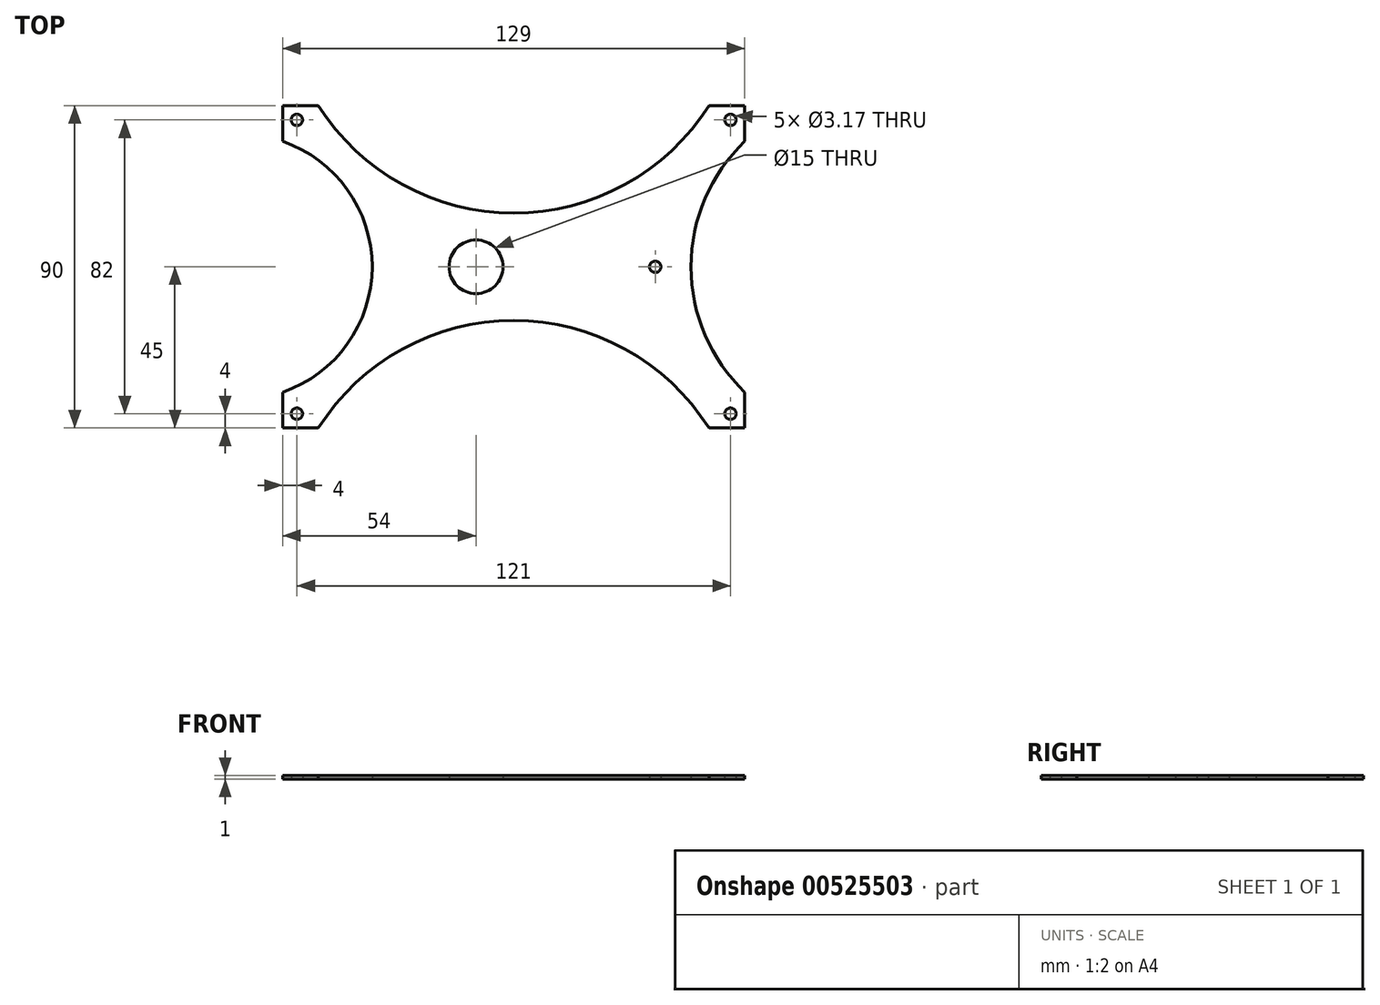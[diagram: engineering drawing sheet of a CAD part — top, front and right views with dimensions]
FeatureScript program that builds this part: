
annotation { "Feature Type Name" : "Feature", "Feature Type Description" : "" }
export const myFeature = defineFeature(function(context is Context, id is Id, definition is map)
    precondition{}
    {
        {
            var Q0;
            Q0=qCreatedBy(makeId("Top.planeOp"),FACE);
            var sketch = newSketch(context, id + "F0", { "sketchPlane" : qUnion([Q0])});
            skLineSegment(sketch, "E0.bottom", {"start": v(75, 45) * mm, "end": v(-75, 45) * mm});
            skLineSegment(sketch, "E0.top", {"start": v(75, -45) * mm, "end": v(-75, -45) * mm});
            skLineSegment(sketch, "E0.left", {"start": v(75, 45) * mm, "end": v(75, -45) * mm});
            skLineSegment(sketch, "E0.right", {"start": v(-75, 45) * mm, "end": v(-75, -45) * mm});
            skPoint(sketch, "E0.middle", {"position": v(0, 0) * mm});
            skCircle(sketch, "E1", {"center": v(0, 0) * mm, "radius": 7.5 * mm});
            skCircle(sketch, "E2", {"center": v(50, 0) * mm, "radius": 1.59 * mm});
            skCircle(sketch, "E3", {"center": v(-50, 41) * mm, "radius": 1.59 * mm});
            skCircle(sketch, "E4", {"center": v(-50, -41) * mm, "radius": 1.59 * mm});
            skCircle(sketch, "E5", {"center": v(71, -41) * mm, "radius": 1.59 * mm});
            skCircle(sketch, "E6", {"center": v(71, 41) * mm, "radius": 1.59 * mm});
            skSolve(sketch);
        }
        {
            var Q0;
            Q0 = qSketchRegion(id + "F0", true);
            extrude(context, id + "F1", {"entities" : qUnion([Q0]), "depth" : 1 * mm, "offsetDistance" : 25 * mm});
        }
        {
            var Q0;
            Q0=qCreatedBy(makeId("Top.planeOp"),FACE);
            var sketch = newSketch(context, id + "F2", { "sketchPlane" : qUnion([Q0])});
            skLineSegment(sketch, "E7.0", {"start": v(75, 45) * mm, "end": v(-75, 45) * mm, "construction": true});
            skLineSegment(sketch, "E8.0", {"start": v(-75, 45) * mm, "end": v(-75, -45) * mm, "construction": true});
            skLineSegment(sketch, "E9.bottom", {"start": v(-75, 45) * mm, "end": v(-54, 45) * mm});
            skLineSegment(sketch, "E9.top", {"start": v(-75, -45) * mm, "end": v(-54, -45) * mm});
            skLineSegment(sketch, "E9.left", {"start": v(-75, 45) * mm, "end": v(-75, -45) * mm});
            skLineSegment(sketch, "E9.right", {"start": v(-54, 45) * mm, "end": v(-54, -45) * mm});
            skCircle(sketch, "E10.0", {"center": v(-50, 41) * mm, "radius": 1.59 * mm, "construction": true});
            skSolve(sketch);
        }
        {
            var Q0;
            Q0 = qSketchRegion(id + "F2", true);
            extrude(context, id + "F3", {"entities" : qUnion([Q0]), "operationType" : NewBodyOperationType.REMOVE, "endBound" : BoundingType.THROUGH_ALL, "depth" : 25 * mm, "offsetDistance" : 25 * mm});
        }
        {
            var Q0;
            Q0=qCreatedBy(makeId("Top.planeOp"),FACE);
            var sketch = newSketch(context, id + "F4", { "sketchPlane" : qUnion([Q0])});
            skLineSegment(sketch, "E11.0", {"start": v(65, 45) * mm, "end": v(-44, 45) * mm});
            skLineSegment(sketch, "E12.0", {"start": v(-54, -35) * mm, "end": v(-54, 35) * mm});
            skLineSegment(sketch, "E13.0", {"start": v(65, -45) * mm, "end": v(-44, -45) * mm});
            skLineSegment(sketch, "E14.0", {"start": v(75, 35) * mm, "end": v(75, -35) * mm});
            skArc(sketch, "E15", {"start": v(-44, 45) * mm, "mid": v(10.5, 15) * mm, "end": v(65, 45) * mm});
            skArc(sketch, "E16", {"start": v(-54, -35) * mm, "mid": v(-29, 0) * mm, "end": v(-54, 35) * mm});
            skArc(sketch, "E17", {"start": v(65, -45) * mm, "mid": v(10.5, -15) * mm, "end": v(-44, -45) * mm});
            skArc(sketch, "E18", {"start": v(75, 35) * mm, "mid": v(60, 0) * mm, "end": v(75, -35) * mm});
            skLineSegment(sketch, "E19", {"start": v(-44, -45) * mm, "end": v(65, -45) * mm});
            skLineSegment(sketch, "E20", {"start": v(75, -35) * mm, "end": v(75, 35) * mm});
            skLineSegment(sketch, "E21", {"start": v(-54, 35) * mm, "end": v(-54, -35) * mm});
            skPoint(sketch, "E22.orphan", {"position": v(-54, 45) * mm});
            skPoint(sketch, "E23.orphan", {"position": v(75, 45) * mm});
            skPoint(sketch, "E24.orphan", {"position": v(75, -45) * mm});
            skPoint(sketch, "E25.orphan", {"position": v(-54, -45) * mm});
            skSolve(sketch);
        }
        {
            var Q0;
            Q0 = qSketchRegion(id + "F4", true);
            extrude(context, id + "F5", {"entities" : qUnion([Q0]), "operationType" : NewBodyOperationType.REMOVE, "depth" : 25 * mm, "offsetDistance" : 25 * mm});
        }
    });
